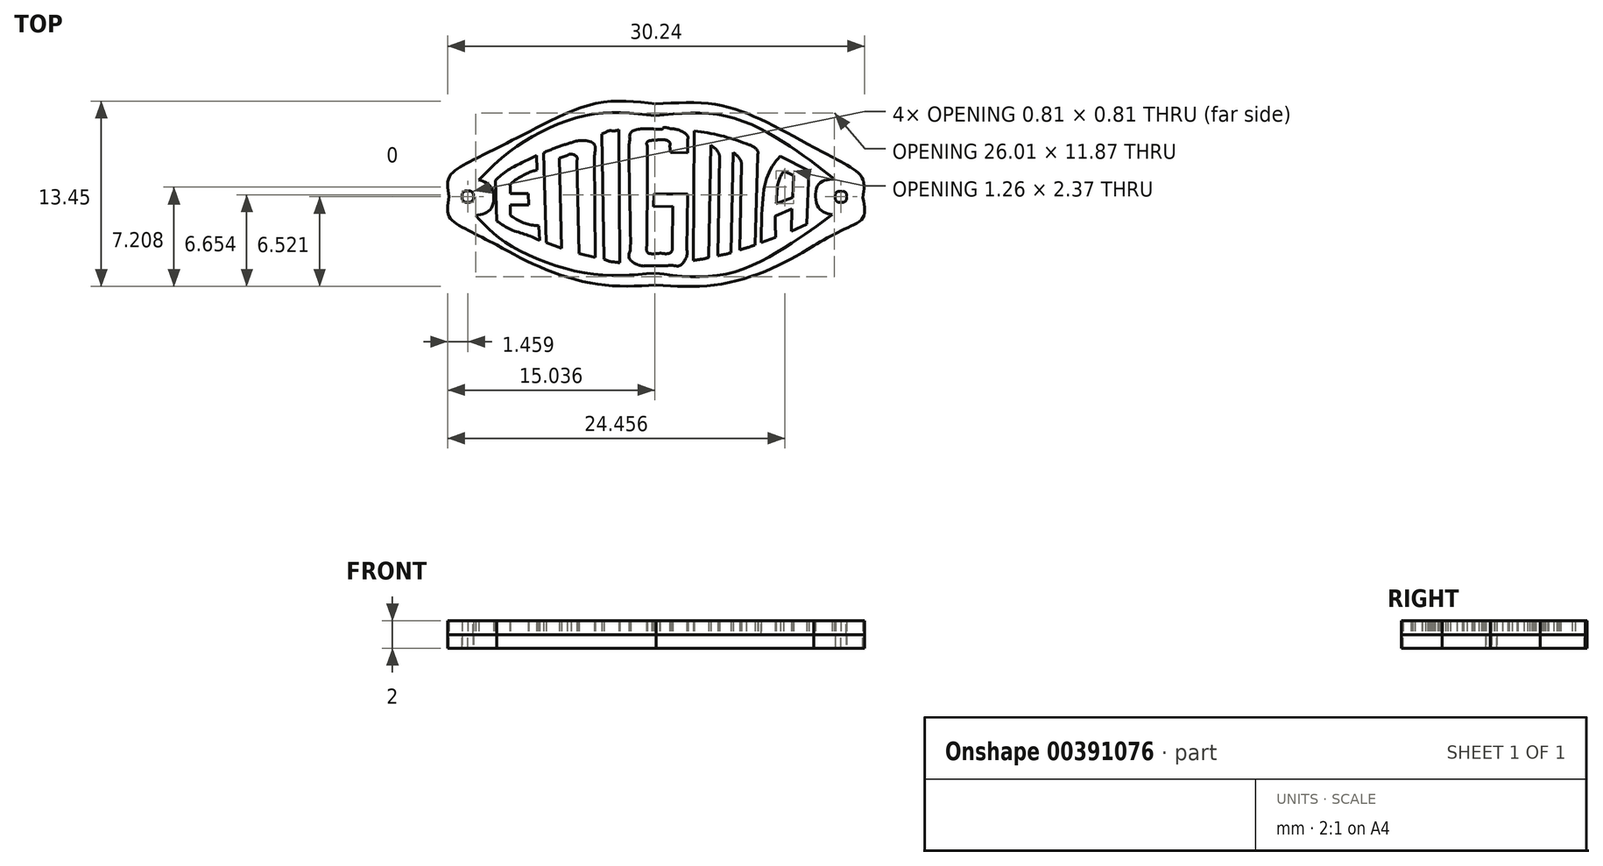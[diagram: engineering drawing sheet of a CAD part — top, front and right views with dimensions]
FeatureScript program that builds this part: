
annotation { "Feature Type Name" : "Feature", "Feature Type Description" : "" }
export const myFeature = defineFeature(function(context is Context, id is Id, definition is map)
    precondition{}
    {
        {
            var Q0;
            Q0=qCreatedBy(makeId("Top.planeOp"),FACE);
            var sketch = newSketch(context, id + "F0", { "sketchPlane" : qUnion([Q0])});
            skFitSpline(sketch, "E0", {"points": [v(-14.97, -0.14) * mm, v(-14.96, 1.26) * mm, v(-13.64, 2.29) * mm, v(-11.55, 3.35) * mm]});
            skFitSpline(sketch, "E1", {"points": [v(-11.55, 3.35) * mm, v(-8.78, 4.75) * mm, v(-4.25, 6.62) * mm, v(0, 6.58) * mm]});
            skFitSpline(sketch, "E2", {"points": [v(0, 6.58) * mm, v(4.26, 6.55) * mm, v(7.6, 5.47) * mm, v(11.52, 3.4) * mm]});
            skFitSpline(sketch, "E3", {"points": [v(11.52, 3.4) * mm, v(13.6, 2.3) * mm, v(15, 1.18) * mm, v(15.03, -0.23) * mm]});
            skFitSpline(sketch, "E4", {"points": [v(15.03, -0.23) * mm, v(15.07, -1.65) * mm, v(13.73, -2.5) * mm, v(11.46, -3.72) * mm]});
            skFitSpline(sketch, "E5", {"points": [v(11.46, -3.72) * mm, v(8.33, -5.41) * mm, v(4.1, -6.59) * mm, v(0.04, -6.56) * mm]});
            skFitSpline(sketch, "E6", {"points": [v(0.04, -6.56) * mm, v(-4.03, -6.53) * mm, v(-8.3, -5.3) * mm, v(-11.5, -3.65) * mm]});
            skFitSpline(sketch, "E7", {"points": [v(-11.5, -3.65) * mm, v(-13.9, -2.43) * mm, v(-14.98, -1.54) * mm, v(-14.97, -0.14) * mm]});
            skFitSpline(sketch, "E8", {"points": [v(9.3, 1.72) * mm, v(8.93, 1) * mm, v(8.8, 0.14) * mm, v(8.76, -0.65) * mm]});
            skLineSegment(sketch, "E9", {"start": v(8.76, -0.65) * mm, "end": v(9.94, -0.2) * mm});
            skLineSegment(sketch, "E10", {"start": v(9.94, -0.2) * mm, "end": v(10.02, 1.36) * mm});
            skLineSegment(sketch, "E11", {"start": v(10.02, 1.36) * mm, "end": v(9.3, 1.72) * mm});
            skLineSegment(sketch, "E12", {"start": v(10.98, -2.16) * mm, "end": v(11.13, 1.71) * mm});
            skLineSegment(sketch, "E13", {"start": v(11.13, 1.71) * mm, "end": v(9.06, 2.78) * mm});
            skLineSegment(sketch, "E14", {"start": v(7.68, -3.48) * mm, "end": v(8.71, -3.1) * mm});
            skLineSegment(sketch, "E15", {"start": v(8.71, -3.1) * mm, "end": v(7.68, -3.48) * mm});
            skFitSpline(sketch, "E16", {"points": [v(7.4, 2.85) * mm, v(7.42, 3.15) * mm, v(7.05, 3.5) * mm, v(6.59, 3.68) * mm]});
            skLineSegment(sketch, "E17", {"start": v(9.89, -1.05) * mm, "end": v(9.87, -2.64) * mm});
            skLineSegment(sketch, "E18", {"start": v(9.87, -2.64) * mm, "end": v(10.98, -2.16) * mm});
            skFitSpline(sketch, "E19", {"points": [v(2.75, -4.78) * mm, v(3.13, -4.72) * mm, v(3.51, -4.67) * mm, v(3.85, -4.57) * mm]});
            skLineSegment(sketch, "E20", {"start": v(2.81, 4.62) * mm, "end": v(2.75, -4.78) * mm});
            skLineSegment(sketch, "E21", {"start": v(2.75, -4.78) * mm, "end": v(2.81, 4.62) * mm});
            skFitSpline(sketch, "E22", {"points": [v(4.53, -4.43) * mm, v(4.84, -4.37) * mm, v(5.13, -4.32) * mm, v(5.47, -4.22) * mm]});
            skLineSegment(sketch, "E23", {"start": v(3.85, -4.57) * mm, "end": v(4, 3.59) * mm});
            skLineSegment(sketch, "E24", {"start": v(4, 3.59) * mm, "end": v(3.85, -4.57) * mm});
            skFitSpline(sketch, "E25", {"points": [v(6.12, -4) * mm, v(6.47, -3.9) * mm, v(6.82, -3.8) * mm, v(7.2, -3.66) * mm]});
            skLineSegment(sketch, "E26", {"start": v(5.47, -4.22) * mm, "end": v(5.64, 3.06) * mm});
            skLineSegment(sketch, "E27", {"start": v(5.64, 3.06) * mm, "end": v(5.47, -4.22) * mm});
            skFitSpline(sketch, "E28", {"points": [v(1.23, -3.7) * mm, v(1.23, -3.98) * mm, v(1.03, -4.25) * mm, v(0.32, -4.25) * mm]});
            skFitSpline(sketch, "E29", {"points": [v(0.32, -4.25) * mm, v(-0.5, -4.25) * mm, v(-0.65, -4) * mm, v(-0.63, -3.74) * mm]});
            skFitSpline(sketch, "E30", {"points": [v(-0.63, -3.74) * mm, v(-0.62, -3.46) * mm, v(-0.6, 3.27) * mm, v(-0.6, 3.54) * mm]});
            skFitSpline(sketch, "E31", {"points": [v(-0.6, 3.54) * mm, v(-0.6, 3.82) * mm, v(-0.04, 3.95) * mm, v(0.29, 3.97) * mm]});
            skFitSpline(sketch, "E32", {"points": [v(0.29, 3.97) * mm, v(0.62, 3.98) * mm, v(1.04, 3.77) * mm, v(1.04, 3.54) * mm]});
            skLineSegment(sketch, "E33", {"start": v(-0.13, -0.87) * mm, "end": v(1.26, -0.85) * mm});
            skLineSegment(sketch, "E34", {"start": v(1.26, -0.85) * mm, "end": v(-0.13, -0.87) * mm});
            skFitSpline(sketch, "E35", {"points": [v(2.33, 3.95) * mm, v(2.31, 4.28) * mm, v(1.6, 4.7) * mm, v(1.09, 4.78) * mm]});
            skFitSpline(sketch, "E36", {"points": [v(1.09, 4.78) * mm, v(0.58, 4.86) * mm, v(0.55, 4.78) * mm, v(-0.27, 4.77) * mm]});
            skFitSpline(sketch, "E37", {"points": [v(-0.27, 4.77) * mm, v(-1.09, 4.75) * mm, v(-1.8, 4.48) * mm, v(-1.86, 3.94) * mm]});
            skFitSpline(sketch, "E38", {"points": [v(-1.86, 3.94) * mm, v(-1.92, 3.4) * mm, v(-1.81, -3.43) * mm, v(-1.84, -4.05) * mm]});
            skFitSpline(sketch, "E39", {"points": [v(-1.84, -4.05) * mm, v(-1.87, -4.67) * mm, v(-1.1, -5.16) * mm, v(-0.59, -5.16) * mm]});
            skFitSpline(sketch, "E40", {"points": [v(-0.59, -5.16) * mm, v(-0.07, -5.16) * mm, v(0.7, -5.16) * mm, v(1.26, -5.14) * mm]});
            skFitSpline(sketch, "E41", {"points": [v(1.26, -5.14) * mm, v(1.81, -5.13) * mm, v(2.27, -4.45) * mm, v(2.28, -4.04) * mm]});
            skLineSegment(sketch, "E42", {"start": v(1.09, 3.05) * mm, "end": v(2.34, 3.03) * mm});
            skLineSegment(sketch, "E43", {"start": v(2.34, 3.03) * mm, "end": v(1.09, 3.05) * mm});
            skLineSegment(sketch, "E44", {"start": v(2.33, 0.05) * mm, "end": v(-0.1, 0.05) * mm});
            skLineSegment(sketch, "E45", {"start": v(-0.1, 0.05) * mm, "end": v(-0.13, -0.87) * mm});
            skFitSpline(sketch, "E46", {"points": [v(-2.66, 4.7) * mm, v(-3.04, 4.6) * mm, v(-3.31, 4.64) * mm, v(-3.88, 4.37) * mm]});
            skLineSegment(sketch, "E47", {"start": v(-2.6, -4.94) * mm, "end": v(-2.66, 4.7) * mm});
            skLineSegment(sketch, "E48", {"start": v(-2.66, 4.7) * mm, "end": v(-2.6, -4.94) * mm});
            skFitSpline(sketch, "E49", {"points": [v(-3.73, -4.69) * mm, v(-3.3, -4.85) * mm, v(-2.95, -4.9) * mm, v(-2.6, -4.94) * mm]});
            skLineSegment(sketch, "E50", {"start": v(-3.88, 4.37) * mm, "end": v(-3.73, -4.69) * mm});
            skLineSegment(sketch, "E51", {"start": v(-3.73, -4.69) * mm, "end": v(-3.88, 4.37) * mm});
            skFitSpline(sketch, "E52", {"points": [v(-4.44, 2.79) * mm, v(-4.47, 3.68) * mm, v(-5.51, 3.91) * mm, v(-6.1, 3.77) * mm]});
            skFitSpline(sketch, "E53", {"points": [v(-6.4, 2.83) * mm, v(-6.12, 2.94) * mm, v(-5.7, 2.73) * mm, v(-5.7, 2.47) * mm]});
            skLineSegment(sketch, "E54", {"start": v(-8.12, 3.03) * mm, "end": v(-7.93, -3.48) * mm});
            skLineSegment(sketch, "E55", {"start": v(-7.93, -3.48) * mm, "end": v(-6.83, -3.89) * mm});
            skLineSegment(sketch, "E56", {"start": v(-6.83, -3.89) * mm, "end": v(-6.98, 2.64) * mm});
            skLineSegment(sketch, "E57", {"start": v(-5.54, -4.28) * mm, "end": v(-4.36, -4.55) * mm});
            skLineSegment(sketch, "E58", {"start": v(-4.36, -4.55) * mm, "end": v(-5.54, -4.28) * mm});
            skFitSpline(sketch, "E59", {"points": [v(-11.5, -1.92) * mm, v(-10.55, -2.52) * mm, v(-9.46, -2.88) * mm, v(-8.41, -3.32) * mm]});
            skLineSegment(sketch, "E60", {"start": v(-11.62, 1.03) * mm, "end": v(-11.5, -1.92) * mm});
            skLineSegment(sketch, "E61", {"start": v(-11.5, -1.92) * mm, "end": v(-11.62, 1.03) * mm});
            skFitSpline(sketch, "E62", {"points": [v(-8.46, -2.27) * mm, v(-9.6, -2.03) * mm, v(-10.53, -1.47) * mm, v(-10.53, -1.37) * mm]});
            skLineSegment(sketch, "E63", {"start": v(-8.41, -3.32) * mm, "end": v(-8.46, -2.27) * mm});
            skLineSegment(sketch, "E64", {"start": v(-8.46, -2.27) * mm, "end": v(-8.41, -3.32) * mm});
            skFitSpline(sketch, "E65", {"points": [v(-10.54, 0.64) * mm, v(-10.54, 0.73) * mm, v(-9.47, 1.46) * mm, v(-8.6, 1.78) * mm]});
            skLineSegment(sketch, "E66", {"start": v(-10.52, -0.74) * mm, "end": v(-9.19, -0.74) * mm});
            skLineSegment(sketch, "E67", {"start": v(-9.19, -0.74) * mm, "end": v(-9.21, 0.08) * mm});
            skLineSegment(sketch, "E68", {"start": v(-9.21, 0.08) * mm, "end": v(-10.53, 0.06) * mm});
            skFitSpline(sketch, "E69", {"points": [v(-8.62, 2.84) * mm, v(-9.6, 2.36) * mm, v(-10.77, 1.72) * mm, v(-11.62, 1.03) * mm]});
            skLineSegment(sketch, "E70", {"start": v(-8.6, 1.78) * mm, "end": v(-8.62, 2.84) * mm});
            skLineSegment(sketch, "E71", {"start": v(-8.62, 2.84) * mm, "end": v(-8.6, 1.78) * mm});
            skFitSpline(sketch, "E72", {"points": [v(-13.04, -1.5) * mm, v(-11.95, -1.05) * mm, v(-11.86, 0.45) * mm, v(-12.8, 1.07) * mm]});
            skFitSpline(sketch, "E73", {"points": [v(-12.8, 1.07) * mm, v(-10.26, 3.34) * mm, v(-5.1, 5.73) * mm, v(-0.01, 5.72) * mm]});
            skFitSpline(sketch, "E74", {"points": [v(-0.01, 5.72) * mm, v(5.07, 5.7) * mm, v(9.73, 3.51) * mm, v(12.97, 1.13) * mm]});
            skFitSpline(sketch, "E75", {"points": [v(12.97, 1.13) * mm, v(11.8, 0.7) * mm, v(11.8, -0.92) * mm, v(12.8, -1.46) * mm]});
            skFitSpline(sketch, "E76", {"points": [v(12.8, -1.46) * mm, v(10.15, -3.35) * mm, v(5.24, -5.74) * mm, v(-0.01, -5.7) * mm]});
            skFitSpline(sketch, "E77", {"points": [v(-0.01, -5.7) * mm, v(-5.26, -5.66) * mm, v(-10.83, -3.49) * mm, v(-13.04, -1.5) * mm]});
            skFitSpline(sketch, "E78", {"points": [v(13.84, -0.16) * mm, v(13.84, -0.38) * mm, v(13.67, -0.55) * mm, v(13.45, -0.55) * mm]});
            skFitSpline(sketch, "E79", {"points": [v(13.45, -0.55) * mm, v(13.23, -0.55) * mm, v(13.06, -0.38) * mm, v(13.06, -0.16) * mm]});
            skFitSpline(sketch, "E80", {"points": [v(13.06, -0.16) * mm, v(13.06, 0.06) * mm, v(13.23, 0.23) * mm, v(13.45, 0.23) * mm]});
            skFitSpline(sketch, "E81", {"points": [v(13.45, 0.23) * mm, v(13.67, 0.23) * mm, v(13.84, 0.06) * mm, v(13.84, -0.16) * mm]});
            skFitSpline(sketch, "E82", {"points": [v(-13.22, -0.15) * mm, v(-13.22, -0.37) * mm, v(-13.4, -0.54) * mm, v(-13.61, -0.54) * mm]});
            skFitSpline(sketch, "E83", {"points": [v(-13.61, -0.54) * mm, v(-13.83, -0.54) * mm, v(-14, -0.37) * mm, v(-14, -0.15) * mm]});
            skFitSpline(sketch, "E84", {"points": [v(-14, -0.15) * mm, v(-14, 0.07) * mm, v(-13.83, 0.24) * mm, v(-13.61, 0.24) * mm]});
            skFitSpline(sketch, "E85", {"points": [v(-13.61, 0.24) * mm, v(-13.4, 0.24) * mm, v(-13.22, 0.07) * mm, v(-13.22, -0.15) * mm]});
            skLineSegment(sketch, "E86", {"start": v(2.33, 0.05) * mm, "end": v(2.28, -4.04) * mm});
            skLineSegment(sketch, "E87", {"start": v(1.26, -0.85) * mm, "end": v(1.23, -3.7) * mm});
            skLineSegment(sketch, "E88", {"start": v(2.33, 3.95) * mm, "end": v(2.34, 3.03) * mm});
            skArc(sketch, "E89", {"start": v(6.59, 3.68) * mm, "mid": v(4.73, 4.28) * mm, "end": v(2.81, 4.62) * mm});
            skLineSegment(sketch, "E90", {"start": v(-10.54, 0.64) * mm, "end": v(-10.53, 0.06) * mm});
            skLineSegment(sketch, "E91", {"start": v(-10.52, -0.74) * mm, "end": v(-10.53, -1.37) * mm});
            skLineSegment(sketch, "E92", {"start": v(-6.98, 2.64) * mm, "end": v(-6.4, 2.83) * mm});
            skLineSegment(sketch, "E93", {"start": v(-5.7, 2.47) * mm, "end": v(-5.54, -4.28) * mm});
            skLineSegment(sketch, "E94", {"start": v(-4.44, 2.79) * mm, "end": v(-4.36, -4.55) * mm});
            skFitSpline(sketch, "E95", {"points": [v(-8.12, 3.03) * mm, v(-7.03, 3.47) * mm, v(-6.1, 3.77) * mm], "startDerivative": vector(2.12, 0.9) * mm, "endDerivative": vector(1.92, 0.58) * mm});
            skFitSpline(sketch, "E96", {"points": [v(4, 3.59) * mm, v(4.18, 3.45) * mm, v(4.21, 3.43) * mm, v(4.28, 3.37) * mm, v(4.46, 3.2) * mm, v(4.6, 2.98) * mm, v(4.63, 2.88) * mm, v(4.64, 2.8) * mm], "startDerivative": vector(1.1, -0.83) * mm, "endDerivative": vector(0.05, -0.6) * mm});
            skLineSegment(sketch, "E97", {"start": v(4.64, 2.8) * mm, "end": v(4.53, -4.43) * mm});
            skFitSpline(sketch, "E98", {"points": [v(5.64, 3.06) * mm, v(6.04, 2.69) * mm, v(6.21, 2.36) * mm, v(6.24, 2.21) * mm], "startDerivative": vector(1.05, -0.84) * mm, "endDerivative": vector(0.05, -0.6) * mm});
            skLineSegment(sketch, "E99", {"start": v(6.24, 2.21) * mm, "end": v(6.12, -4) * mm});
            skLineSegment(sketch, "E100", {"start": v(7.4, 2.85) * mm, "end": v(7.2, -3.66) * mm});
            skLineSegment(sketch, "E101", {"start": v(8.7, -1.56) * mm, "end": v(9.89, -1.05) * mm});
            skFitSpline(sketch, "E102", {"points": [v(8.71, -3.1) * mm, v(8.7, -2.33) * mm, v(8.7, -1.64) * mm, v(8.7, -1.56) * mm, v(8.7, -1.56) * mm], "startDerivative": vector(-0.06, 1.75) * mm, "endDerivative": vector(0.12, 0.1) * mm});
            skFitSpline(sketch, "E103", {"points": [v(7.68, -3.48) * mm, v(7.7, -1.86) * mm, v(7.84, 0.2) * mm, v(8.08, 1.25) * mm, v(8.49, 2.08) * mm, v(8.95, 2.68) * mm, v(9.06, 2.78) * mm], "startDerivative": vector(-0.02, 7.18) * mm, "endDerivative": vector(1.43, 1.15) * mm});
            skLineSegment(sketch, "E104", {"start": v(1.04, 3.54) * mm, "end": v(1.09, 3.05) * mm});
            skSolve(sketch);
        }
        {
            var Q0;
            Q0=makeQuery(id+"F0.imprint","IMPRINT",FACE,{"disambiguationData":[TD([[makeQuery(id+"F0.imprint","IMPRINT",EDGE,{"derivedFrom":sQuery(id+"F0.wireOp",EDGE,"E0")}),-1.0]])]});
            var Q1;
            Q1=makeQuery(id+"F0.imprint","IMPRINT",FACE,{"disambiguationData":[TD([[makeQuery(id+"F0.imprint","IMPRINT",EDGE,{"derivedFrom":sQuery(id+"F0.wireOp",EDGE,"E59")}),1.0]])]});
            var Q2;
            Q2=makeQuery(id+"F0.imprint","IMPRINT",FACE,{"disambiguationData":[TD([[makeQuery(id+"F0.imprint","IMPRINT",EDGE,{"derivedFrom":sQuery(id+"F0.wireOp",EDGE,"E52")}),1.0]])]});
            var Q3;
            Q3=makeQuery(id+"F0.imprint","IMPRINT",FACE,{"disambiguationData":[TD([[makeQuery(id+"F0.imprint","IMPRINT",EDGE,{"derivedFrom":sQuery(id+"F0.wireOp",EDGE,"E46")}),1.0]])]});
            var Q4;
            Q4=makeQuery(id+"F0.imprint","IMPRINT",FACE,{"disambiguationData":[TD([[makeQuery(id+"F0.imprint","IMPRINT",EDGE,{"derivedFrom":sQuery(id+"F0.wireOp",EDGE,"E28")}),1.0]])]});
            var Q5;
            Q5=makeQuery(id+"F0.imprint","IMPRINT",FACE,{"disambiguationData":[TD([[makeQuery(id+"F0.imprint","IMPRINT",EDGE,{"derivedFrom":sQuery(id+"F0.wireOp",EDGE,"E16")}),1.0]])]});
            var Q6;
            Q6=makeQuery(id+"F0.imprint","IMPRINT",FACE,{"disambiguationData":[TD([[makeQuery(id+"F0.imprint","IMPRINT",EDGE,{"derivedFrom":sQuery(id+"F0.wireOp",EDGE,"E8")}),-1.0]])]});
            extrude(context, id + "F1", {"entities" : qUnion([Q0, Q1, Q2, Q3, Q4, Q5, Q6]), "depth" : 1 * mm});
        }
        {
            var Q0;
            Q0=makeQuery(id+"F0.imprint","IMPRINT",FACE,{"disambiguationData":[TD([[makeQuery(id+"F0.imprint","IMPRINT",EDGE,{"derivedFrom":sQuery(id+"F0.wireOp",EDGE,"E0")}),-1.0]])]});
            var Q1;
            Q1=makeQuery(id+"F0.imprint","IMPRINT",FACE,{"disambiguationData":[TD([[makeQuery(id+"F0.imprint","IMPRINT",EDGE,{"derivedFrom":sQuery(id+"F0.wireOp",EDGE,"E12")}),-1.0]])]});
            var Q2;
            Q2=makeQuery(id+"F0.imprint","IMPRINT",FACE,{"disambiguationData":[TD([[makeQuery(id+"F0.imprint","IMPRINT",EDGE,{"derivedFrom":sQuery(id+"F0.wireOp",EDGE,"E59")}),1.0]])]});
            var Q3;
            Q3=makeQuery(id+"F0.imprint","IMPRINT",FACE,{"disambiguationData":[TD([[makeQuery(id+"F0.imprint","IMPRINT",EDGE,{"derivedFrom":sQuery(id+"F0.wireOp",EDGE,"E52")}),1.0]])]});
            var Q4;
            Q4=makeQuery(id+"F0.imprint","IMPRINT",FACE,{"disambiguationData":[TD([[makeQuery(id+"F0.imprint","IMPRINT",EDGE,{"derivedFrom":sQuery(id+"F0.wireOp",EDGE,"E46")}),1.0]])]});
            var Q5;
            Q5=makeQuery(id+"F0.imprint","IMPRINT",FACE,{"disambiguationData":[TD([[makeQuery(id+"F0.imprint","IMPRINT",EDGE,{"derivedFrom":sQuery(id+"F0.wireOp",EDGE,"E28")}),1.0]])]});
            var Q6;
            Q6=makeQuery(id+"F0.imprint","IMPRINT",FACE,{"disambiguationData":[TD([[makeQuery(id+"F0.imprint","IMPRINT",EDGE,{"derivedFrom":sQuery(id+"F0.wireOp",EDGE,"E16")}),1.0]])]});
            var Q7;
            Q7=makeQuery(id+"F0.imprint","IMPRINT",FACE,{"disambiguationData":[TD([[makeQuery(id+"F0.imprint","IMPRINT",EDGE,{"derivedFrom":sQuery(id+"F0.wireOp",EDGE,"E8")}),-1.0]])]});
            var Q8;
            Q8=makeQuery(id+"F0.imprint","IMPRINT",FACE,{"disambiguationData":[TD([[makeQuery(id+"F0.imprint","IMPRINT",EDGE,{"derivedFrom":sQuery(id+"F0.wireOp",EDGE,"E8")}),1.0]])]});
            extrude(context, id + "F2", {"entities" : qUnion([Q0, Q1, Q2, Q3, Q4, Q5, Q6, Q7, Q8]), "oppositeDirection" : true, "depth" : 1 * mm});
        }
    });
